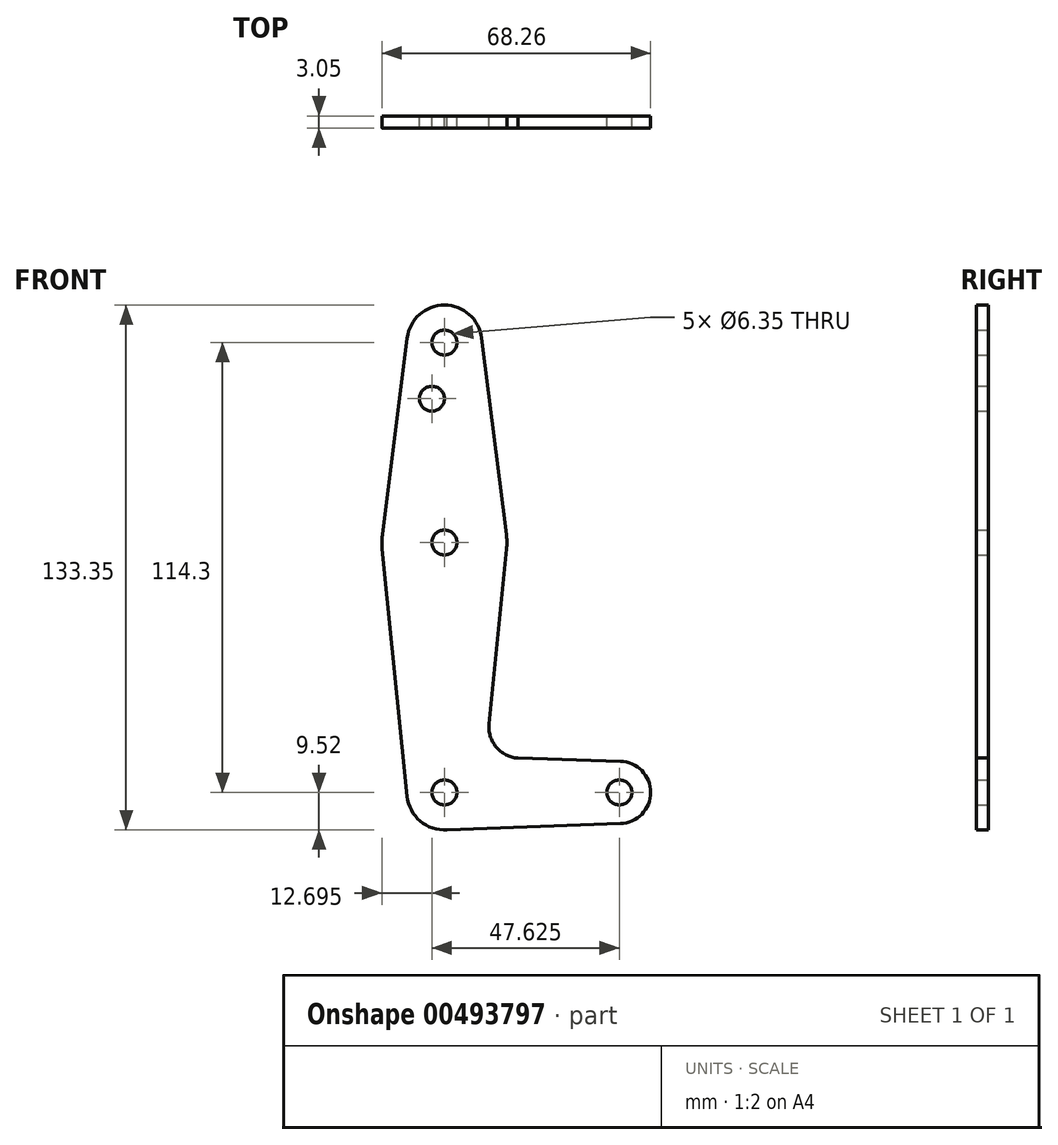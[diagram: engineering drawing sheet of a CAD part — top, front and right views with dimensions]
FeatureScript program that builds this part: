
annotation { "Feature Type Name" : "Feature", "Feature Type Description" : "" }
export const myFeature = defineFeature(function(context is Context, id is Id, definition is map)
    precondition{}
    {
        {
            var Q0;
            Q0=qCreatedBy(makeId("Front.planeOp"),FACE);
            var sketch = newSketch(context, id + "F0", { "sketchPlane" : qUnion([Q0])});
            skLineSegment(sketch, "E0", {"start": v(44.45, 0) * mm, "end": v(3.17, 0) * mm});
            skCircle(sketch, "E1", {"center": v(0, 114.3) * mm, "radius": 9.53 * mm});
            skCircle(sketch, "E2", {"center": v(44.45, 0) * mm, "radius": 7.94 * mm});
            skLineSegment(sketch, "E3", {"start": v(0, 3.17) * mm, "end": v(0, 114.3) * mm});
            skCircle(sketch, "E4", {"center": v(0, 63.5) * mm, "radius": 15.88 * mm});
            skLineSegment(sketch, "E5", {"start": v(9.45, 115.5) * mm, "end": v(15.75, 65.48) * mm});
            skLineSegment(sketch, "E6", {"start": v(-9.45, 115.5) * mm, "end": v(-15.75, 65.48) * mm});
            skLineSegment(sketch, "E7", {"start": v(15.8, 61.91) * mm, "end": v(11.33, 17.45) * mm});
            skLineSegment(sketch, "E8", {"start": v(-15.8, 61.91) * mm, "end": v(-9.48, -0.95) * mm});
            skLineSegment(sketch, "E9", {"start": v(44.7, 7.93) * mm, "end": v(18.67, 8.73) * mm});
            skLineSegment(sketch, "E10", {"start": v(44.7, -7.93) * mm, "end": v(0, -9.53) * mm});
            skCircle(sketch, "E11", {"center": v(0, 114.3) * mm, "radius": 3.18 * mm});
            skCircle(sketch, "E12", {"center": v(0, 63.5) * mm, "radius": 3.18 * mm});
            skArc(sketch, "E13", {"start": v(0, 3.18) * mm, "mid": v(-2.25, -2.25) * mm, "end": v(3.18, 0) * mm});
            skCircle(sketch, "E14", {"center": v(44.45, 0) * mm, "radius": 3.18 * mm});
            skCircle(sketch, "E15", {"center": v(-3.18, 100.03) * mm, "radius": 3.18 * mm});
            skArc(sketch, "E16", {"start": v(11.33, 17.45) * mm, "mid": v(13.15, 11.54) * mm, "end": v(18.67, 8.73) * mm});
            skArc(sketch, "E17.trimOffspring", {"start": v(-9.48, -0.95) * mm, "mid": v(-6.13, -7.29) * mm, "end": v(0.68, -9.5) * mm});
            skArc(sketch, "E18", {"start": v(3.18, 0) * mm, "mid": v(2.25, 2.25) * mm, "end": v(0, 3.18) * mm});
            skSolve(sketch);
        }
        {
            var Q0;
            Q0 = qSketchRegion(id + "F0", true);
            extrude(context, id + "F1", {"entities" : qUnion([Q0]), "depth" : 3.05 * mm});
        }
    });
